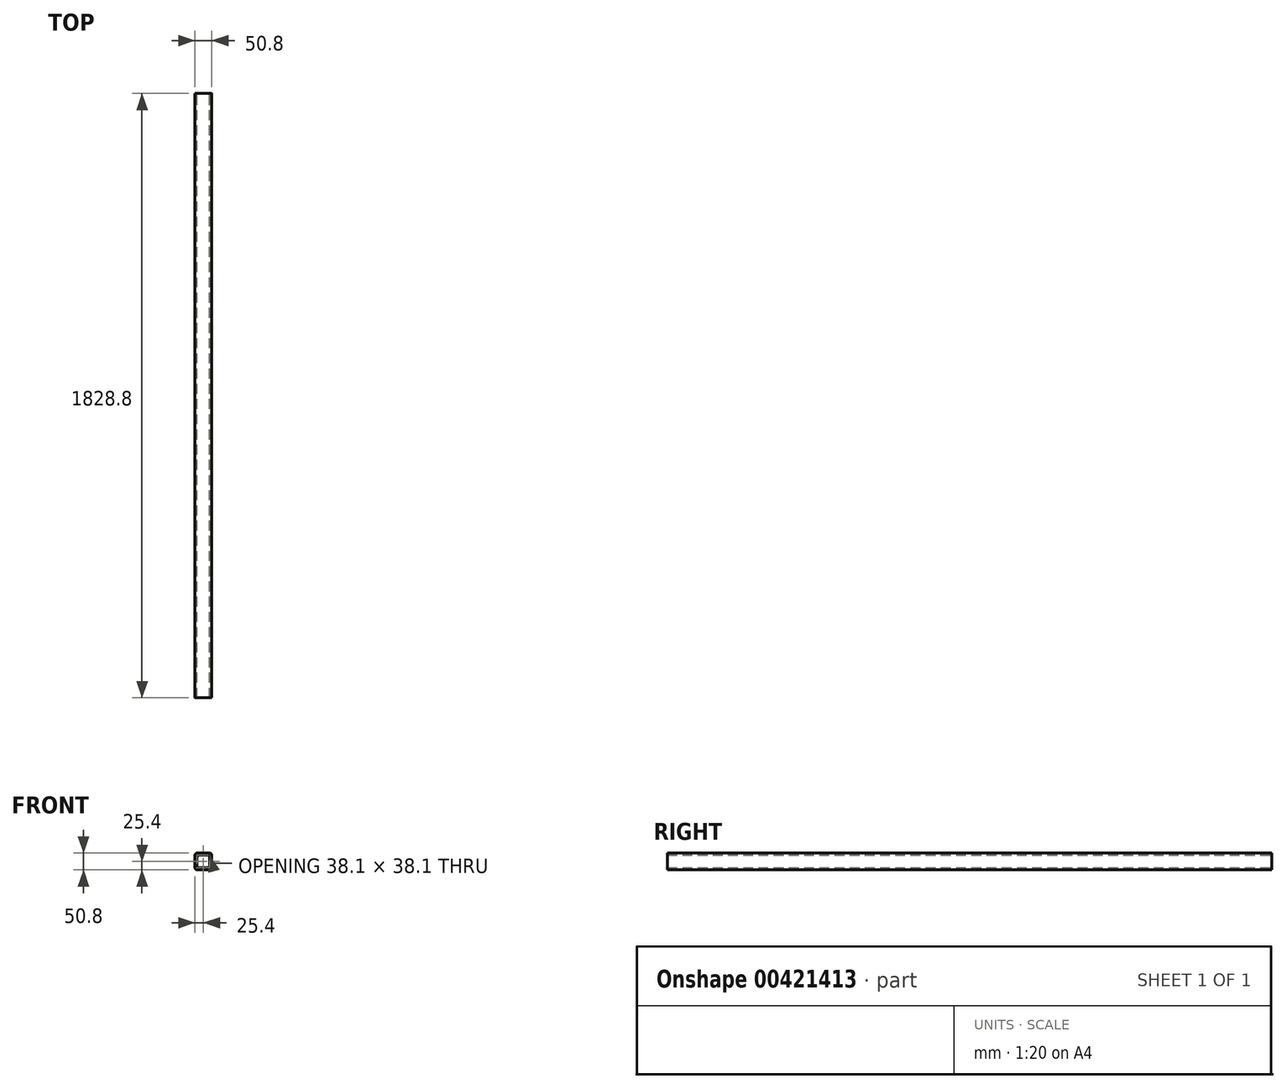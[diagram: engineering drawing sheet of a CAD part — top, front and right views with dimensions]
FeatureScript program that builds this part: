
annotation { "Feature Type Name" : "Feature", "Feature Type Description" : "" }
export const myFeature = defineFeature(function(context is Context, id is Id, definition is map)
    precondition{}
    {
        {
            var Q0;
            Q0=qCreatedBy(makeId("Front.planeOp"),FACE);
            var sketch = newSketch(context, id + "F0", { "sketchPlane" : qUnion([Q0])});
            skLineSegment(sketch, "E0.bottom", {"start": v(19.05, -19.05) * mm, "end": v(-19.05, -19.05) * mm});
            skLineSegment(sketch, "E0.top", {"start": v(19.05, 19.05) * mm, "end": v(-19.05, 19.05) * mm});
            skLineSegment(sketch, "E0.left", {"start": v(19.05, -19.05) * mm, "end": v(19.05, 19.05) * mm});
            skLineSegment(sketch, "E0.right", {"start": v(-19.05, -19.05) * mm, "end": v(-19.05, 19.05) * mm});
            skPoint(sketch, "E0.middle", {"position": v(0, 0) * mm});
            skLineSegment(sketch, "E1.bottom", {"start": v(25.4, -25.4) * mm, "end": v(-25.4, -25.4) * mm});
            skLineSegment(sketch, "E1.top", {"start": v(25.4, 25.4) * mm, "end": v(-25.4, 25.4) * mm});
            skLineSegment(sketch, "E1.left", {"start": v(25.4, -25.4) * mm, "end": v(25.4, 25.4) * mm});
            skLineSegment(sketch, "E1.right", {"start": v(-25.4, -25.4) * mm, "end": v(-25.4, 25.4) * mm});
            skSolve(sketch);
        }
        {
            var Q0;
            Q0 = qSketchRegion(id + "F0", true);
            extrude(context, id + "F1", {"entities" : qUnion([Q0]), "endBound" : BoundingType.SYMMETRIC, "depth" : 1828.8 * mm});
        }
        {
            var Q0;
            Q0=makeQuery(id+"F1.opExtrude","SWEPT_EDGE",EDGE,{"disambiguationData":[OSD([sQuery(id+"F0.wireOp",EDGE,"E0.top"),sQuery(id+"F0.wireOp",EDGE,"E0.right")])]});
            var Q1;
            Q1=makeQuery(id+"F1.opExtrude","SWEPT_EDGE",EDGE,{"disambiguationData":[OSD([sQuery(id+"F0.wireOp",EDGE,"E1.bottom"),sQuery(id+"F0.wireOp",EDGE,"E1.left")])]});
            var Q2;
            Q2=makeQuery(id+"F1.opExtrude","SWEPT_EDGE",EDGE,{"disambiguationData":[OSD([sQuery(id+"F0.wireOp",EDGE,"E1.bottom"),sQuery(id+"F0.wireOp",EDGE,"E1.right")])]});
            var Q3;
            Q3=makeQuery(id+"F1.opExtrude","SWEPT_EDGE",EDGE,{"disambiguationData":[OSD([sQuery(id+"F0.wireOp",EDGE,"E1.top"),sQuery(id+"F0.wireOp",EDGE,"E1.left")])]});
            var Q4;
            Q4=makeQuery(id+"F1.opExtrude","SWEPT_EDGE",EDGE,{"disambiguationData":[OSD([sQuery(id+"F0.wireOp",EDGE,"E0.bottom"),sQuery(id+"F0.wireOp",EDGE,"E0.left")])]});
            var Q5;
            Q5=makeQuery(id+"F1.opExtrude","SWEPT_EDGE",EDGE,{"disambiguationData":[OSD([sQuery(id+"F0.wireOp",EDGE,"E1.top"),sQuery(id+"F0.wireOp",EDGE,"E1.right")])]});
            var Q6;
            Q6=makeQuery(id+"F1.opExtrude","SWEPT_EDGE",EDGE,{"disambiguationData":[OSD([sQuery(id+"F0.wireOp",EDGE,"E0.top"),sQuery(id+"F0.wireOp",EDGE,"E0.left")])]});
            var Q7;
            Q7=makeQuery(id+"F1.opExtrude","SWEPT_EDGE",EDGE,{"disambiguationData":[OSD([sQuery(id+"F0.wireOp",EDGE,"E0.bottom"),sQuery(id+"F0.wireOp",EDGE,"E0.right")])]});
            fillet(context, id + "F2", {"entities" : qUnion([Q0, Q1, Q2, Q3, Q4, Q5, Q6, Q7]), "radius" : 6.35 * mm, "tangentPropagation" : true, "allowEdgeOverflow" : false});
        }
    });
